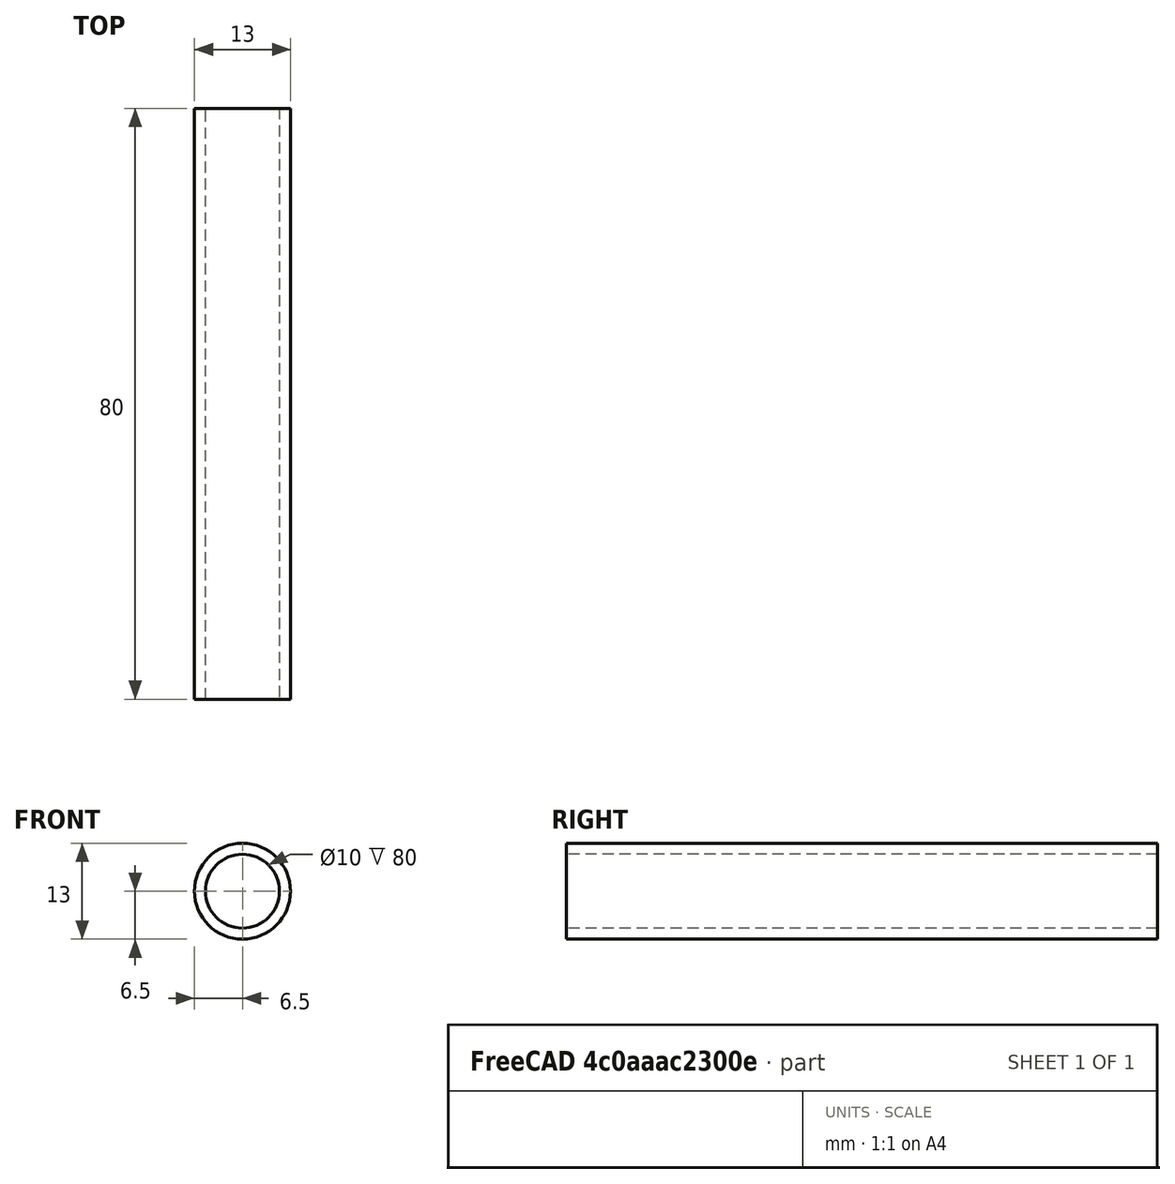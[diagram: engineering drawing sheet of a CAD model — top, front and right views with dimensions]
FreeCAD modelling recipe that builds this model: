
FCSTD DOCUMENT  (FreeCAD 0.18.4R)
Label: tube_long
Comment: # 2020-02-12 13:38:34: read from <userpath>/repositories/sussex_neuro/Olfactometer/hardware/mechanics/from_raiser_et_al/tube_long.ipt
License: All rights reserved
LicenseURL: http://en.wikipedia.org/wiki/All_rights_reserved
objects: Sketcher::SketchObject×2, Spreadsheet::Sheet×1, Part::Extrusion×1
note: 3 computed .brp shape members not serialized (recipe doc carries the construction recipe); baked Part::Feature solids carry a one-line shape summary decoded from their .brp

FEATURE [Spreadsheet::Sheet] Parameters
  cells = A1=Parameter; B1=Value; C1=Fromula; D1=Tolerance; E1=Comment; A2=d10; B2(d10_)=0.3; C2=0.3mm; D2=NOMINAL; A3=d11; B3(d11_)=0.3; C3=0.3mm; D3=NOMINAL; A4=d12; B4(d12_)=0.5; C4=0.5mm; D4=NOMINAL; A5=d13; B5(d13_)=2; C5=2mm; D5=NOMINAL; A6=d14; B6(d14_)=0; C6=0mm; D6=NOMINAL; A7=d15; B7(d15_)=20; C7=20mm; D7=NOMINAL; A8=d4; B8(d4_)=13; C8=13mm; D8=NOMINAL; A9=d6; B9(d6_)=10; C9=10mm; D9=NOMINAL; A10=d7; B10(d7_)=80; C10=80mm; D10=NOMINAL; A11=d8; B11(d8_)=0; C11=0°; D11=NOMINAL; A12=d9; B12(d9_)=0.3; C12=0.3mm; D12=NOMINAL
FEATURE [Sketcher::SketchObject] Sketch3
  Placement = pos=(0,0,0) rot=(0,0.707107,0.707107;3.14159rad)
  sketch-geometry (2):
    g0: Circle CenterX=0 CenterY=0 CenterZ=0 NormalX=0 NormalY=0 NormalZ=1 AngleXU=0 Radius=6.5
    g1: Circle CenterX=0 CenterY=0 CenterZ=0 NormalX=0 NormalY=0 NormalZ=1 AngleXU=0 Radius=5
  constraints (2):
    c: Radius(g0) = 6.5  'd4'
    c: Radius(g1) = 5  'd6'
FEATURE [Sketcher::SketchObject] Sketch3_bp
  Placement = pos=(0,0,0) rot=(0,0.707107,0.707107;3.14159rad)
  sketch-geometry (2):
    g0: Circle CenterX=0 CenterY=0 CenterZ=0 NormalX=0 NormalY=0 NormalZ=1 AngleXU=0 Radius=6.5
    g1: Circle CenterX=0 CenterY=0 CenterZ=0 NormalX=0 NormalY=0 NormalZ=1 AngleXU=0 Radius=5
FEATURE [Part::Extrusion] Extrusion2
  Base = -> Sketch3_bp
  Dir = (0,1,0)
  DirMode = 0
  FaceMakerClass = Part::FaceMakerBullseye
  LengthFwd = 80
  LengthRev = 0
  Solid = true
  Symmetric = false
  expr: LengthFwd = Parameters.d7_
  expr: TaperAngle = Parameters.d8_
